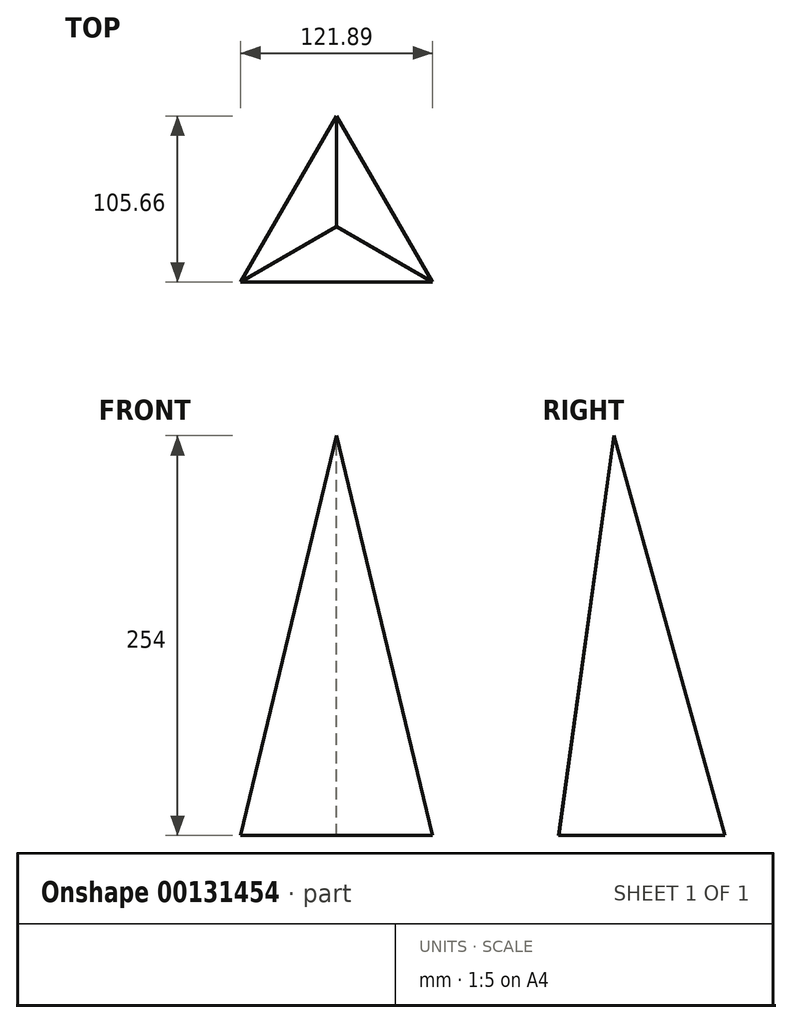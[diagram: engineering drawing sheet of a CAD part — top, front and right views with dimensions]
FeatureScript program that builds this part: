
annotation { "Feature Type Name" : "Feature", "Feature Type Description" : "" }
export const myFeature = defineFeature(function(context is Context, id is Id, definition is map)
    precondition{}
    {
        {
            var Q0;
            Q0=qCreatedBy(makeId("Top.planeOp"),FACE);
            var sketch = newSketch(context, id + "F0", { "sketchPlane" : qUnion([Q0])});
            skCircle(sketch, "E0.cCircle", {"center": v(0, 0) * mm, "radius": 70.38 * mm, "construction": true});
            skLineSegment(sketch, "E0.0", {"start": v(-60.9, -35.28) * mm, "end": v(-0.1, 70.38) * mm});
            skLineSegment(sketch, "E0.1", {"start": v(-0.1, 70.38) * mm, "end": v(61, -35.1) * mm});
            skLineSegment(sketch, "E0.2", {"start": v(61, -35.1) * mm, "end": v(-60.9, -35.28) * mm});
            skSolve(sketch);
        }
        {
            var Q0;
            Q0=qCreatedBy(makeId("Top.planeOp"),FACE);
            cPlane(context, id + "F1", {"entities" : qUnion([Q0]), "cplaneType" : CPlaneType.OFFSET, "offset" : 254 * mm, "width" : 152.4 * mm, "height" : 152.4 * mm});
        }
        {
            var Q0;
            Q0=qCreatedBy(id+"F1.planeOp",FACE);
            var sketch = newSketch(context, id + "F2", { "sketchPlane" : qUnion([Q0])});
            skPoint(sketch, "E1", {"position": v(0, 0) * mm});
            skSolve(sketch);
        }
        {
            var Q0;
            Q0=makeQuery(id+"F0.imprint","IMPRINT",FACE,{"disambiguationData":[TD([[makeQuery(id+"F0.imprint","IMPRINT",EDGE,{"derivedFrom":sQuery(id+"F0.wireOp",EDGE,"E0.0")}),-1.0]])]});
            var Q1;
            Q1=sQuery(id+"F2.wireOp",VERTEX,"E1");
            loft(context, id + "F3", {"sheetProfilesArray" : [{ "sheetProfileEntities" : qUnion([Q0]) }, { "sheetProfileEntities" : qUnion([Q1]) }]});
        }
    });
